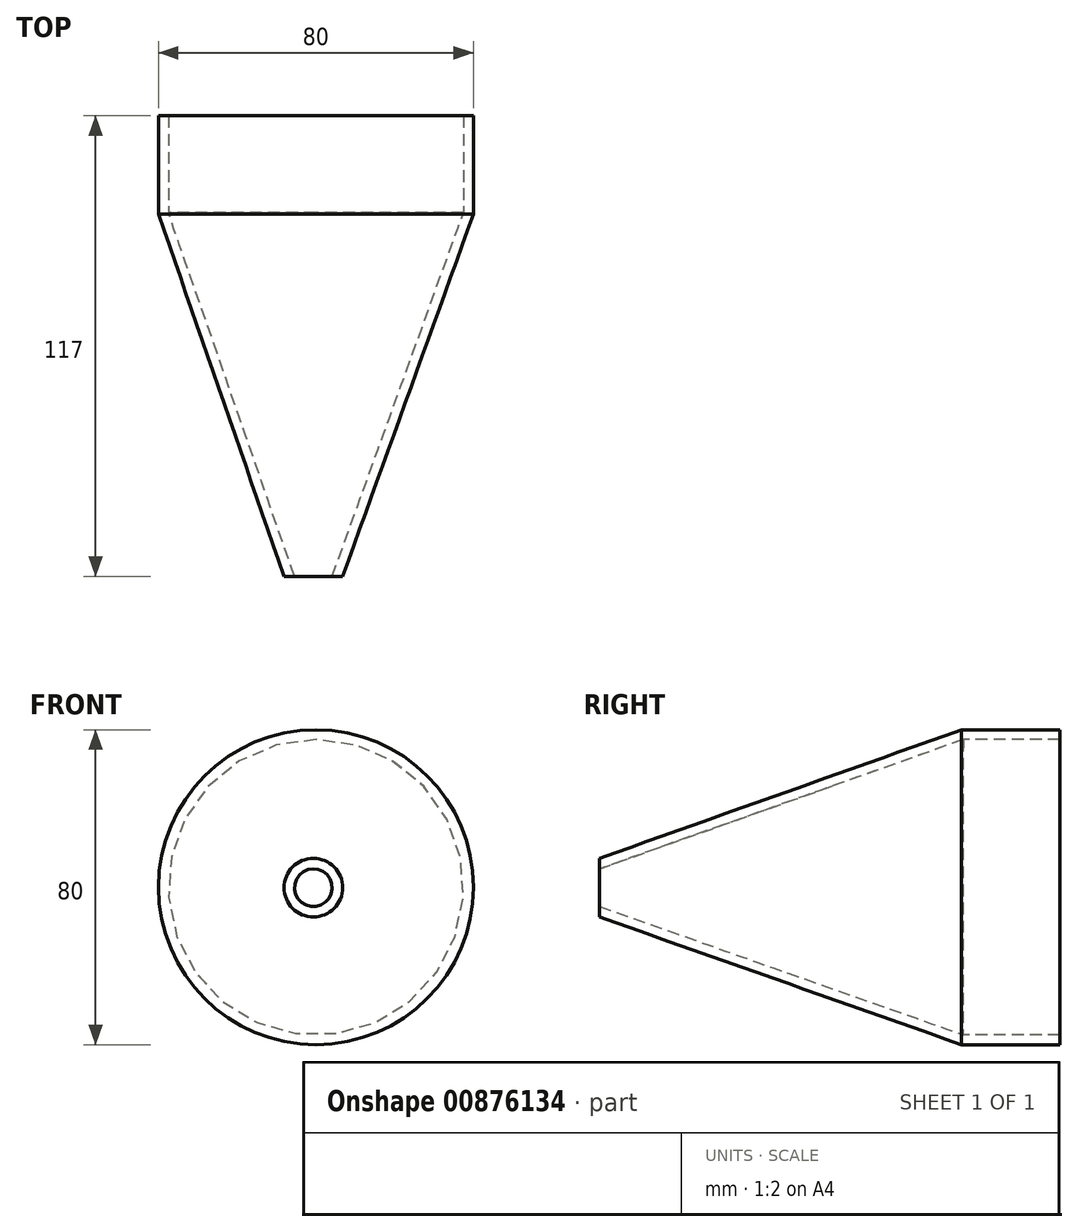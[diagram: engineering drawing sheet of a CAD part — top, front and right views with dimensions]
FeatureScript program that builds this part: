
annotation { "Feature Type Name" : "Feature", "Feature Type Description" : "" }
export const myFeature = defineFeature(function(context is Context, id is Id, definition is map)
    precondition{}
    {
        {
            var Q0;
            Q0=qCreatedBy(makeId("Front.planeOp"),FACE);
            var sketch = newSketch(context, id + "F0", { "sketchPlane" : qUnion([Q0])});
            skCircle(sketch, "E0", {"center": v(0, 0) * mm, "radius": 40 * mm});
            skSolve(sketch);
        }
        {
            var Q0;
            Q0=qCreatedBy(makeId("Front.planeOp"),FACE);
            cPlane(context, id + "F1", {"entities" : qUnion([Q0]), "cplaneType" : CPlaneType.OFFSET, "offset" : 92 * mm, "width" : 150 * mm, "height" : 150 * mm});
        }
        {
            var Q0;
            Q0=qCreatedBy(id+"F1.planeOp",FACE);
            var sketch = newSketch(context, id + "F2", { "sketchPlane" : qUnion([Q0])});
            skCircle(sketch, "E1", {"center": v(-0.66, -0.11) * mm, "radius": 7.44 * mm});
            skSolve(sketch);
        }
        {
            var Q0;
            Q0=makeQuery(id+"F0.imprint","IMPRINT",FACE,{"disambiguationData":[TD([[makeQuery(id+"F0.imprint","IMPRINT",EDGE,{"derivedFrom":sQuery(id+"F0.wireOp",EDGE,"E0")}),1.0]])]});
            var Q1;
            Q1=makeQuery(id+"F2.imprint","IMPRINT",FACE,{"disambiguationData":[TD([[makeQuery(id+"F2.imprint","IMPRINT",EDGE,{"derivedFrom":sQuery(id+"F2.wireOp",EDGE,"E1")}),1.0]])]});
            loft(context, id + "F3", {"sheetProfilesArray" : [{ "sheetProfileEntities" : qUnion([Q0]) }, { "sheetProfileEntities" : qUnion([Q1]) }]});
        }
        {
            var Q0;
            Q0=makeQuery(id+"F3.opLoft","CAP_FACE",FACE,{"disambiguationData":[OSD([makeQuery(id+"F0.imprint","IMPRINT",FACE,{"disambiguationData":[TD([[makeQuery(id+"F0.imprint","IMPRINT",EDGE,{"derivedFrom":sQuery(id+"F0.wireOp",EDGE,"E0")}),1.0]])]})])],"isStart":true});
            extrude(context, id + "F4", {"entities" : qUnion([Q0]), "operationType" : NewBodyOperationType.ADD, "depth" : 25 * mm, "offsetDistance" : 25 * mm});
        }
        {
            var Q0;
            Q0=makeQuery(id+"F4.opExtrude","CAP_FACE",FACE,{"disambiguationData":[OSD([makeQuery(id+"F0.imprint","IMPRINT",FACE,{"disambiguationData":[TD([[makeQuery(id+"F0.imprint","IMPRINT",EDGE,{"derivedFrom":sQuery(id+"F0.wireOp",EDGE,"E0")}),1.0]])]})])],"isStart":false});
            shell(context, id + "F5", {"entities" : qUnion([Q0]), "thickness" : 2.5 * mm});
        }
        {
            var Q0;
            Q0=makeQuery(id+"F3.opLoft","CAP_FACE",FACE,{"disambiguationData":[OSD([makeQuery(id+"F2.imprint","IMPRINT",FACE,{"disambiguationData":[TD([[makeQuery(id+"F2.imprint","IMPRINT",EDGE,{"derivedFrom":sQuery(id+"F2.wireOp",EDGE,"E1")}),1.0]])]})])],"isStart":true});
            var Q1;
            Q1=makeQuery(id+"F5.opShell","OFFSET_FACE",FACE,{"disambiguationData":[OSD([makeQuery(id+"F2.imprint","IMPRINT",FACE,{"disambiguationData":[TD([[makeQuery(id+"F2.imprint","IMPRINT",EDGE,{"derivedFrom":sQuery(id+"F2.wireOp",EDGE,"E1")}),1.0]])]})])]});
            shell(context, id + "F6", {"entities" : qUnion([Q0, Q1]), "thickness" : 2.5 * mm});
        }
    });
